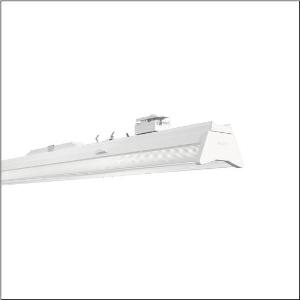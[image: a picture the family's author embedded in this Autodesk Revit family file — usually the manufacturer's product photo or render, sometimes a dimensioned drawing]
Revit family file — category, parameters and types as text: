
# Revit family: licross_11_performance_mo_51tm167n485g
name_source: partatom
category: Lighting Fixtures
units: mm (PartAtom-declared; Revit-internal decimal feet)

## family parameters
Cut with Voids When Loaded = No
Host = Face
Light Source = No
Part Type = Normal
Room Calculation Point = No
Round Connector Dimension = Use Diameter
Shared = No

## types (1)
- Licross 11 Performance MO (1 x LED, 8840 lm, 48.6 W, 4000K)
    Apparent Load = 49 VA
    CIE Flux Codes = 66 88 96 79 100
    Color Rendering = 80
    Color Temperature = 4000K
    Default Elevation = 1800 mm
    Description = Licross 11 Performance MO, luminaire insert, of sheet steel, galvanised, coil coated, white, length: 1.500mm, width: 120mm, height: 123mm, LED rated luminous flux: 8.840lm, light colour: 840, SDCM (Standard Deviation of Colour Matching)MacAdam ≤ 2 SDCM (initial), control gear: ON/OFF, with plug, 3-pole, with phase selection, mains connection: 220..240V, AC, 50/60Hz, rated input power: 49W, internal wiring halogen-free, primary light control with lens, of plastic, primary optical cover: cover, of PMMA, light emission: direct/indirect distribution, primary light characteristic: symmetric, protection rating (complete): IP40, insulation class (complete): insulation class I (protective earthing), certification: CE, ENEC, VDE, UKCA, protection symbol: D if used in an environment without relevant dust loads with corresponding accessories, impact resistance: IK06, permissible ambient temperature for indoor applications: -25..+35°C, corresponds to IFS (International Featured Standards) requirements for safety and quality in the food industry, reducing of maximum allowable ambient temperature of 5°C with ceiling mounting, LABS conformity tested according to VDMA 24364:2018-05, The light source and the operating device comply with the requirements of the Ecodesign Regulation (EU) 2019/2020 and are replaceable in accordance with this regulation, packaging unit: 1 piece
    Height = 114 mm
    Lamp = 1 x LED
    Lamp Light Flux = 8840 lm
    Lamp Power = 48.6 W
    Lamp count = 1
    Length = 1500 mm
    Luminous efficacy = 182 lm/W
    Manufacturer = Siteco
    ModVariant = No
    Model = 51TM167N485G
    Mounting Place = Ceiling
    Mounting Type = Pendant
    Number of Poles = 1
    OnlyDefault = Yes
    Power Factor = 1
    Product Name = Licross 11 Performance MO
    Product group = luminaire insert | ceiling pendant
    ProductGroupID = 901
    Protection Class = Protection class I
    Protection Degree = IP 40
    RLX_Detail_Level = 1
    RLX_Emergency_Light_Flux = 0 lm
    RLX_Emergency_Type = 0
    RLX_Emergency_Type_DB = No
    RlxData = <blob elided: 30637 chars, md5=c5e2376f>
    Socket = socket
    Standby Power = 0 W
    System Light Flux = 8840 lm
    System Power = 49 W
    Type Comments = Product without accessories
    Type Image = l_1256138.jpg
    URL = http://relux.com
    VarID = ---
    Voltage = 0 V
    Weight = 0.00 kg
    Width = 120 mm

## geometry (parser evidence)
native form markers: Blend x4, Sweep x12
no freeform markers — native parametric forms only
